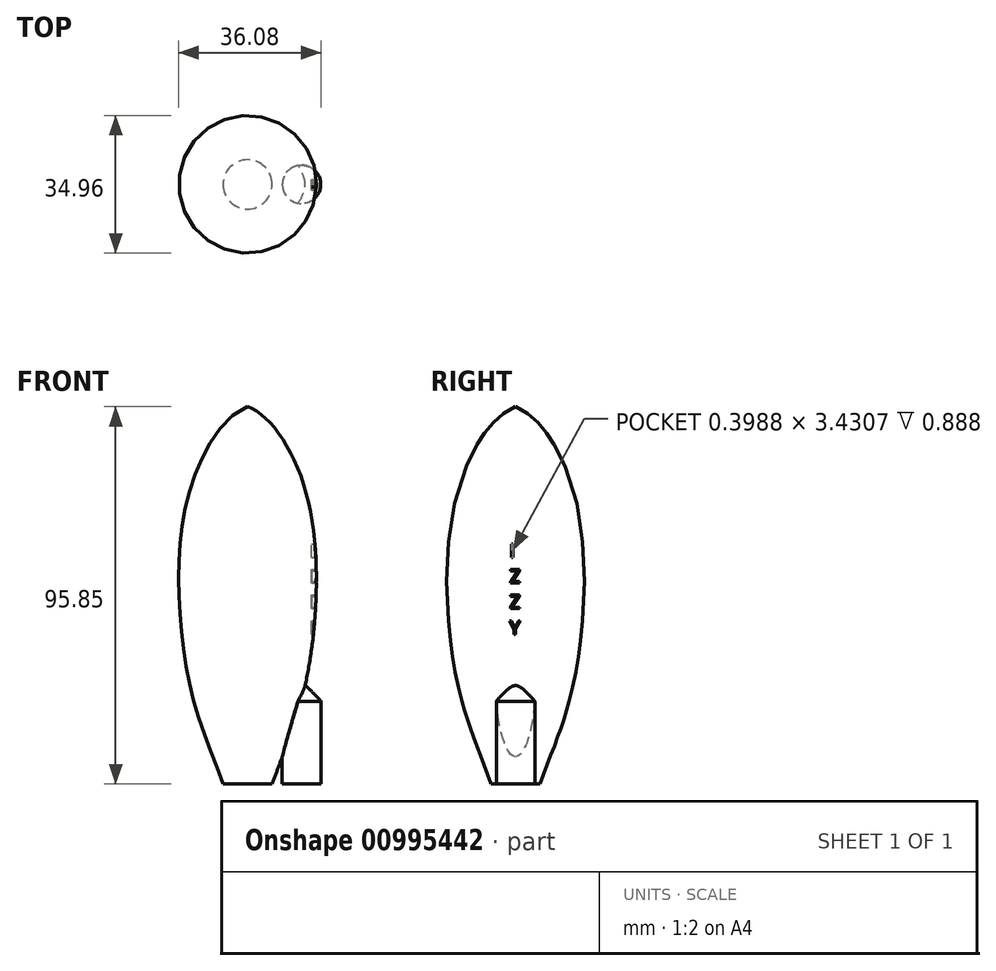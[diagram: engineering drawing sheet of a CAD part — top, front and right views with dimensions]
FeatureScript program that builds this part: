
annotation { "Feature Type Name" : "Feature", "Feature Type Description" : "" }
export const myFeature = defineFeature(function(context is Context, id is Id, definition is map)
    precondition{}
    {
        {
            var Q0;
            Q0=qCreatedBy(makeId("Front.planeOp"),FACE);
            var sketch = newSketch(context, id + "F0", { "sketchPlane" : qUnion([Q0])});
            skLineSegment(sketch, "E0", {"start": v(0, 0) * mm, "end": v(0, 100) * mm, "construction": true});
            skLineSegment(sketch, "E1", {"start": v(15, 0) * mm, "end": v(15, 100) * mm, "construction": true});
            skLineSegment(sketch, "E2", {"start": v(15, 100) * mm, "end": v(0, 100) * mm, "construction": true});
            skFitSpline(sketch, "E3", {"points": [v(6.26, 0) * mm, v(15, 26.77) * mm, v(15, 73.51) * mm, v(0, 95.85) * mm], "startDerivative": vector(41.3, 113.6) * mm, "endDerivative": vector(-57.56, 19.72) * mm});
            skLineSegment(sketch, "E4", {"start": v(0, 95.85) * mm, "end": v(0, 0) * mm});
            skLineSegment(sketch, "E5", {"start": v(6.26, 0) * mm, "end": v(0, 0) * mm});
            skSolve(sketch);
        }
        {
            var Q0;
            Q0 = qSketchRegion(id + "F0", true);
            var Q1;
            Q1=sQuery(id+"F0.wireOp",EDGE,"E0");
            revolve(context, id + "F1", {"surfaceOperationType" : NewSurfaceOperationType.NEW, "entities" : qUnion([Q0]), "axis" : qUnion([Q1]), "revolveType" : RevolveType.FULL});
        }
        {
            var Q0;
            Q0=qCreatedBy(makeId("Top.planeOp"),FACE);
            var sketch = newSketch(context, id + "F2", { "sketchPlane" : qUnion([Q0])});
            skCircle(sketch, "E6", {"center": v(13.71, 0) * mm, "radius": 4.89 * mm});
            skSolve(sketch);
        }
        {
            var Q0;
            Q0 = qSketchRegion(id + "F2", true);
            extrude(context, id + "F3", {"entities" : qUnion([Q0]), "operationType" : NewBodyOperationType.ADD, "depth" : 25 * mm, "offsetDistance" : 25 * mm});
        }
        {
            var Q0;
            Q0=makeQuery(id+"F3.opExtrude","CAP_EDGE",EDGE,{"disambiguationData":[OSD([sQuery(id+"F2.wireOp",EDGE,"E6")])],"isStart":false});
            fillet(context, id + "F4", {"entities" : qUnion([Q0]), "radius" : 4 * mm, "rho" : 0.05, "crossSection" : FilletCrossSection.CONIC, "allowEdgeOverflow" : false});
        }
        {
            var Q0;
            Q0=qCreatedBy(makeId("Right.planeOp"),FACE);
            cPlane(context, id + "F5", {"entities" : qUnion([Q0]), "cplaneType" : CPlaneType.OFFSET, "offset" : 20 * mm, "width" : 150 * mm, "height" : 150 * mm});
        }
        {
            var Q0;
            Q0=qCreatedBy(id+"F5.planeOp",FACE);
            var sketch = newSketch(context, id + "F6", { "sketchPlane" : qUnion([Q0])});
            skText(sketch, "E7", { "text": "I\nZ\nZ\nY", "fontName": "OpenSans-Regular.ttf"});
            const initialGuessF6  = {"E7": [-0.0015, 0.0576, 1, 0, 0.00346]};
            skSetInitialGuess(sketch, initialGuessF6);
            skSolve(sketch);
        }
        {
            var Q0;
            Q0 = qSketchRegion(id + "F6", true);
            extrude(context, id + "F7", {"entities" : qUnion([Q0]), "operationType" : NewBodyOperationType.REMOVE, "oppositeDirection" : true, "depth" : 3.8 * mm, "offsetDistance" : 25 * mm});
        }
    });
